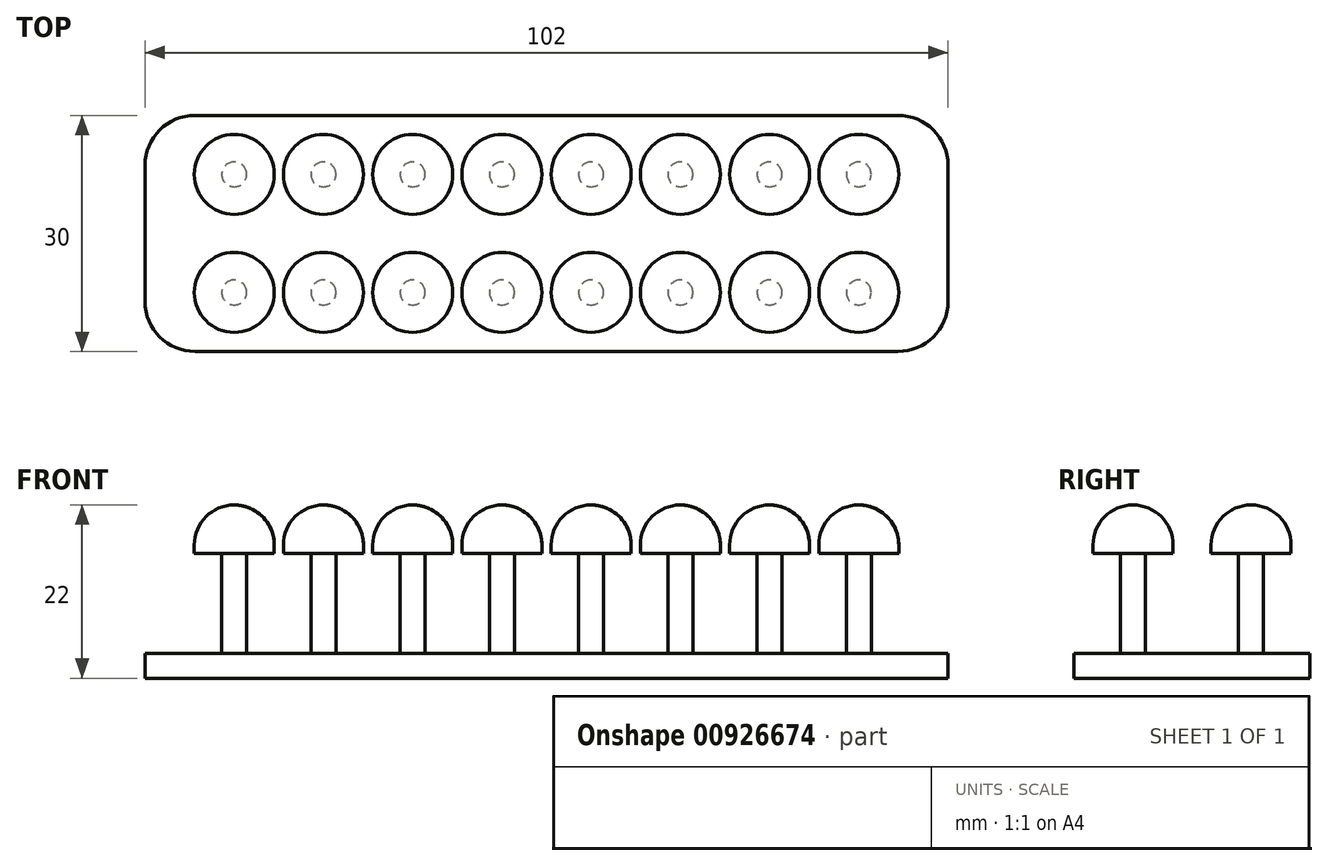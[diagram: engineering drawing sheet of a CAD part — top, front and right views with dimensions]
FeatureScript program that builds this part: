
annotation { "Feature Type Name" : "Feature", "Feature Type Description" : "" }
export const myFeature = defineFeature(function(context is Context, id is Id, definition is map)
    precondition{}
    {
        {
            var Q0;
            Q0=qCreatedBy(makeId("Top.planeOp"),FACE);
            var sketch = newSketch(context, id + "F0", { "sketchPlane" : qUnion([Q0])});
            skLineSegment(sketch, "E0.bottom", {"start": v(44.65, -15) * mm, "end": v(-44.65, -15) * mm});
            skLineSegment(sketch, "E0.top", {"start": v(44.65, 15) * mm, "end": v(-44.65, 15) * mm});
            skLineSegment(sketch, "E0.left", {"start": v(51, -8.65) * mm, "end": v(51, 8.65) * mm});
            skLineSegment(sketch, "E0.right", {"start": v(-51, -8.65) * mm, "end": v(-51, 8.65) * mm});
            skPoint(sketch, "E0.middle", {"position": v(0, 0) * mm});
            skPoint(sketch, "E1.visualSharp", {"position": v(-51, 15) * mm});
            skArc(sketch, "E1.filletArc", {"start": v(-44.65, 15) * mm, "mid": v(-49.14, 13.14) * mm, "end": v(-51, 8.65) * mm});
            skPoint(sketch, "E2.visualSharp", {"position": v(-51, -15) * mm});
            skArc(sketch, "E2.filletArc", {"start": v(-51, -8.65) * mm, "mid": v(-49.14, -13.14) * mm, "end": v(-44.65, -15) * mm});
            skPoint(sketch, "E3.visualSharp", {"position": v(51, 15) * mm});
            skArc(sketch, "E3.filletArc", {"start": v(51, 8.65) * mm, "mid": v(49.14, 13.14) * mm, "end": v(44.65, 15) * mm});
            skPoint(sketch, "E4.visualSharp", {"position": v(51, -15) * mm});
            skArc(sketch, "E4.filletArc", {"start": v(44.65, -15) * mm, "mid": v(49.14, -13.14) * mm, "end": v(51, -8.65) * mm});
            skSolve(sketch);
        }
        {
            var Q0;
            Q0 = qSketchRegion(id + "F0", true);
            extrude(context, id + "F1", {"entities" : qUnion([Q0]), "depth" : 3.17 * mm, "offsetDistance" : 25.4 * mm});
        }
        {
            var Q0;
            Q0=makeQuery(id+"F1.opExtrude","CAP_FACE",FACE,{"disambiguationData":[OSD([sQuery(id+"F0.wireOp",EDGE,"E0.bottom"),sQuery(id+"F0.wireOp",EDGE,"E0.top"),sQuery(id+"F0.wireOp",EDGE,"E0.left"),sQuery(id+"F0.wireOp",EDGE,"E0.right"),sQuery(id+"F0.wireOp",EDGE,"E1.filletArc"),sQuery(id+"F0.wireOp",EDGE,"E2.filletArc"),sQuery(id+"F0.wireOp",EDGE,"E3.filletArc"),sQuery(id+"F0.wireOp",EDGE,"E4.filletArc")])],"isStart":false});
            var sketch = newSketch(context, id + "F2", { "sketchPlane" : qUnion([Q0])});
            skCircle(sketch, "E5", {"center": v(-39.67, 7.5) * mm, "radius": 1.59 * mm});
            skCircle(sketch, "E6", {"center": v(-28.33, 7.5) * mm, "radius": 1.59 * mm});
            skCircle(sketch, "E7", {"center": v(-17, 7.5) * mm, "radius": 1.59 * mm});
            skCircle(sketch, "E8", {"center": v(-5.67, 7.5) * mm, "radius": 1.59 * mm});
            skCircle(sketch, "E9", {"center": v(5.67, 7.5) * mm, "radius": 1.59 * mm});
            skCircle(sketch, "E10", {"center": v(17, 7.5) * mm, "radius": 1.59 * mm});
            skCircle(sketch, "E11", {"center": v(28.33, 7.5) * mm, "radius": 1.59 * mm});
            skCircle(sketch, "E12", {"center": v(39.67, 7.5) * mm, "radius": 1.59 * mm});
            skCircle(sketch, "E13", {"center": v(-39.67, -7.5) * mm, "radius": 1.59 * mm});
            skCircle(sketch, "E14", {"center": v(-28.33, -7.5) * mm, "radius": 1.59 * mm});
            skCircle(sketch, "E15", {"center": v(-17, -7.5) * mm, "radius": 1.59 * mm});
            skCircle(sketch, "E16", {"center": v(-5.67, -7.5) * mm, "radius": 1.59 * mm});
            skCircle(sketch, "E17", {"center": v(5.67, -7.5) * mm, "radius": 1.59 * mm});
            skCircle(sketch, "E18", {"center": v(17, -7.5) * mm, "radius": 1.59 * mm});
            skCircle(sketch, "E19", {"center": v(28.33, -7.5) * mm, "radius": 1.59 * mm});
            skCircle(sketch, "E20", {"center": v(39.67, -7.5) * mm, "radius": 1.59 * mm});
            skSolve(sketch);
        }
        {
            var Q0;
            Q0 = qSketchRegion(id + "F2", true);
            extrude(context, id + "F3", {"entities" : qUnion([Q0]), "operationType" : NewBodyOperationType.ADD, "depth" : 12.7 * mm, "offsetDistance" : 25.4 * mm});
        }
        {
            var Q0;
            Q0=makeQuery(id+"F3.opExtrude","CAP_FACE",FACE,{"disambiguationData":[OSD([sQuery(id+"F2.wireOp",EDGE,"E5")])],"isStart":false});
            var sketch = newSketch(context, id + "F4", { "sketchPlane" : qUnion([Q0])});
            skCircle(sketch, "E21", {"center": v(-39.67, 7.5) * mm, "radius": 5.08 * mm});
            skCircle(sketch, "E22", {"center": v(-28.33, 7.5) * mm, "radius": 5.08 * mm});
            skCircle(sketch, "E23", {"center": v(-17, 7.5) * mm, "radius": 5.08 * mm});
            skCircle(sketch, "E24", {"center": v(-5.67, 7.5) * mm, "radius": 5.08 * mm});
            skCircle(sketch, "E25", {"center": v(5.67, 7.5) * mm, "radius": 5.08 * mm});
            skCircle(sketch, "E26", {"center": v(17, 7.5) * mm, "radius": 5.08 * mm});
            skCircle(sketch, "E27", {"center": v(28.33, 7.5) * mm, "radius": 5.08 * mm});
            skCircle(sketch, "E28", {"center": v(39.67, 7.5) * mm, "radius": 5.08 * mm});
            skCircle(sketch, "E29", {"center": v(-39.67, -7.5) * mm, "radius": 5.08 * mm});
            skCircle(sketch, "E30", {"center": v(-28.33, -7.5) * mm, "radius": 5.08 * mm});
            skCircle(sketch, "E31", {"center": v(-17, -7.5) * mm, "radius": 5.08 * mm});
            skCircle(sketch, "E32", {"center": v(-5.67, -7.5) * mm, "radius": 5.08 * mm});
            skCircle(sketch, "E33", {"center": v(5.67, -7.5) * mm, "radius": 5.08 * mm});
            skCircle(sketch, "E34", {"center": v(17, -7.5) * mm, "radius": 5.08 * mm});
            skCircle(sketch, "E35", {"center": v(28.33, -7.5) * mm, "radius": 5.08 * mm});
            skCircle(sketch, "E36", {"center": v(39.67, -7.5) * mm, "radius": 5.08 * mm});
            skSolve(sketch);
        }
        {
            var Q0;
            Q0 = qSketchRegion(id + "F4", true);
            extrude(context, id + "F5", {"entities" : qUnion([Q0]), "operationType" : NewBodyOperationType.ADD, "depth" : 6.13 * mm, "offsetDistance" : 25.4 * mm});
        }
        {
            var Q0;
            Q0=makeQuery(id+"F5.opExtrude","CAP_EDGE",EDGE,{"disambiguationData":[OSD([sQuery(id+"F4.wireOp",EDGE,"E21")])],"isStart":false});
            var Q1;
            Q1=makeQuery(id+"F5.opExtrude","CAP_EDGE",EDGE,{"disambiguationData":[OSD([sQuery(id+"F4.wireOp",EDGE,"E22")])],"isStart":false});
            var Q2;
            Q2=makeQuery(id+"F5.opExtrude","CAP_EDGE",EDGE,{"disambiguationData":[OSD([sQuery(id+"F4.wireOp",EDGE,"E23")])],"isStart":false});
            var Q3;
            Q3=makeQuery(id+"F5.opExtrude","CAP_EDGE",EDGE,{"disambiguationData":[OSD([sQuery(id+"F4.wireOp",EDGE,"E24")])],"isStart":false});
            var Q4;
            Q4=makeQuery(id+"F5.opExtrude","CAP_EDGE",EDGE,{"disambiguationData":[OSD([sQuery(id+"F4.wireOp",EDGE,"E25")])],"isStart":false});
            var Q5;
            Q5=makeQuery(id+"F5.opExtrude","CAP_EDGE",EDGE,{"disambiguationData":[OSD([sQuery(id+"F4.wireOp",EDGE,"E26")])],"isStart":false});
            var Q6;
            Q6=makeQuery(id+"F5.opExtrude","CAP_EDGE",EDGE,{"disambiguationData":[OSD([sQuery(id+"F4.wireOp",EDGE,"E27")])],"isStart":false});
            var Q7;
            Q7=makeQuery(id+"F5.opExtrude","CAP_EDGE",EDGE,{"disambiguationData":[OSD([sQuery(id+"F4.wireOp",EDGE,"E28")])],"isStart":false});
            var Q8;
            Q8=makeQuery(id+"F5.opExtrude","CAP_EDGE",EDGE,{"disambiguationData":[OSD([sQuery(id+"F4.wireOp",EDGE,"E36")])],"isStart":false});
            var Q9;
            Q9=makeQuery(id+"F5.opExtrude","CAP_EDGE",EDGE,{"disambiguationData":[OSD([sQuery(id+"F4.wireOp",EDGE,"E35")])],"isStart":false});
            var Q10;
            Q10=makeQuery(id+"F5.opExtrude","CAP_EDGE",EDGE,{"disambiguationData":[OSD([sQuery(id+"F4.wireOp",EDGE,"E34")])],"isStart":false});
            var Q11;
            Q11=makeQuery(id+"F5.opExtrude","CAP_EDGE",EDGE,{"disambiguationData":[OSD([sQuery(id+"F4.wireOp",EDGE,"E33")])],"isStart":false});
            var Q12;
            Q12=makeQuery(id+"F5.opExtrude","CAP_EDGE",EDGE,{"disambiguationData":[OSD([sQuery(id+"F4.wireOp",EDGE,"E32")])],"isStart":false});
            var Q13;
            Q13=makeQuery(id+"F5.opExtrude","CAP_EDGE",EDGE,{"disambiguationData":[OSD([sQuery(id+"F4.wireOp",EDGE,"E31")])],"isStart":false});
            var Q14;
            Q14=makeQuery(id+"F5.opExtrude","CAP_EDGE",EDGE,{"disambiguationData":[OSD([sQuery(id+"F4.wireOp",EDGE,"E30")])],"isStart":false});
            var Q15;
            Q15=makeQuery(id+"F5.opExtrude","CAP_EDGE",EDGE,{"disambiguationData":[OSD([sQuery(id+"F4.wireOp",EDGE,"E29")])],"isStart":false});
            fillet(context, id + "F6", {"entities" : qUnion([Q0, Q1, Q2, Q3, Q4, Q5, Q6, Q7, Q8, Q9, Q10, Q11, Q12, Q13, Q14, Q15]), "radius" : 5.08 * mm, "tangentPropagation" : true, "allowEdgeOverflow" : false});
        }
    });
